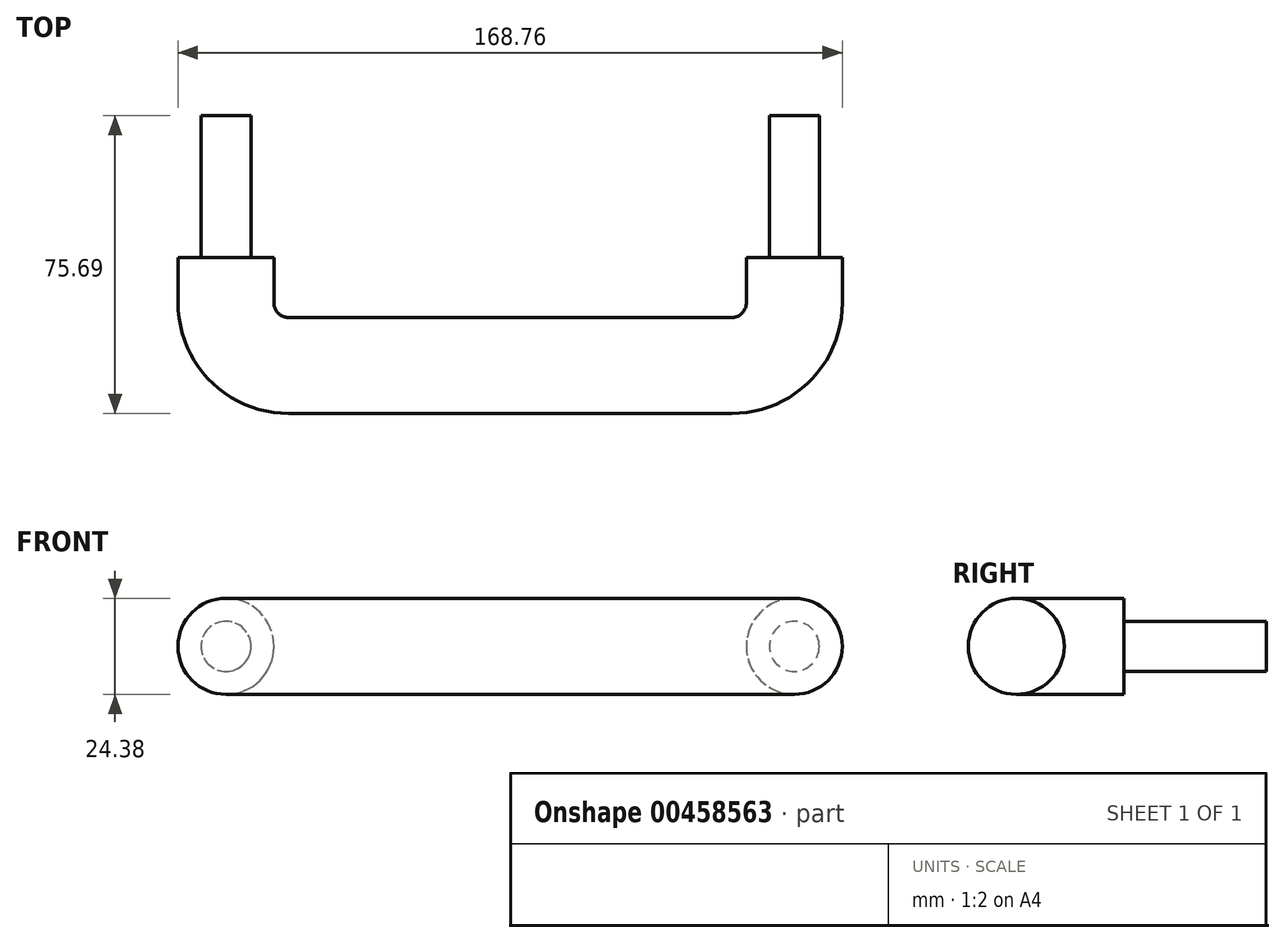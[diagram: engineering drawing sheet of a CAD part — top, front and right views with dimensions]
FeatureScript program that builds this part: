
annotation { "Feature Type Name" : "Feature", "Feature Type Description" : "" }
export const myFeature = defineFeature(function(context is Context, id is Id, definition is map)
    precondition{}
    {
        {
            var Q0;
            Q0=qCreatedBy(makeId("Top.planeOp"),FACE);
            var sketch = newSketch(context, id + "F0", { "sketchPlane" : qUnion([Q0])});
            skLineSegment(sketch, "E0", {"start": v(-72.19, 27.38) * mm, "end": v(-72.19, 15.87) * mm});
            skLineSegment(sketch, "E1", {"start": v(-56.31, 0) * mm, "end": v(56.31, 0) * mm});
            skLineSegment(sketch, "E2", {"start": v(72.19, 15.87) * mm, "end": v(72.19, 27.38) * mm});
            skLineSegment(sketch, "E3", {"start": v(-72.19, 27.38) * mm, "end": v(-72.19, 63.5) * mm});
            skLineSegment(sketch, "E4", {"start": v(-72.19, 63.5) * mm, "end": v(72.19, 63.5) * mm});
            skLineSegment(sketch, "E5", {"start": v(72.19, 27.38) * mm, "end": v(72.19, 63.5) * mm});
            skPoint(sketch, "E6.visualSharp", {"position": v(-72.19, 0) * mm});
            skArc(sketch, "E6.filletArc", {"start": v(-72.19, 15.87) * mm, "mid": v(-67.54, 4.65) * mm, "end": v(-56.31, 0) * mm});
            skPoint(sketch, "E7.visualSharp", {"position": v(72.19, 0) * mm});
            skArc(sketch, "E7.filletArc", {"start": v(56.31, 0) * mm, "mid": v(67.54, 4.65) * mm, "end": v(72.19, 15.87) * mm});
            skLineSegment(sketch, "E8", {"start": v(-72.19, 27.38) * mm, "end": v(72.19, 27.38) * mm, "construction": true});
            skSolve(sketch);
        }
        {
            var Q0;
            Q0=sQuery(id+"F0.wireOp",VERTEX,"E0.start");
            var Q1;
            Q1=sQuery(id+"F0.wireOp",EDGE,"E0");
            cPlane(context, id + "F1", {"entities" : qUnion([Q0, Q1]), "cplaneType" : CPlaneType.LINE_POINT, "offset" : 25.4 * mm, "width" : 152.4 * mm, "height" : 152.4 * mm});
        }
        {
            var Q0;
            Q0=qCreatedBy(id+"F1.planeOp",FACE);
            var sketch = newSketch(context, id + "F2", { "sketchPlane" : qUnion([Q0])});
            skCircle(sketch, "E9", {"center": v(72.19, 0) * mm, "radius": 12.2 * mm});
            skCircle(sketch, "E10", {"center": v(-72.19, 0) * mm, "radius": 6.35 * mm});
            skSolve(sketch);
        }
        {
            var Q0;
            Q0=makeQuery(id+"F2.imprint","IMPRINT",FACE,{"disambiguationData":[TD([[makeQuery(id+"F2.imprint","IMPRINT",EDGE,{"derivedFrom":sQuery(id+"F2.wireOp",EDGE,"E9")}),1.0]])]});
            var Q1;
            Q1=sQuery(id+"F0.wireOp",EDGE,"E2");
            var Q2;
            Q2=sQuery(id+"F0.wireOp",EDGE,"E7.filletArc");
            var Q3;
            Q3=sQuery(id+"F0.wireOp",EDGE,"E1");
            var Q4;
            Q4=sQuery(id+"F0.wireOp",EDGE,"E6.filletArc");
            var Q5;
            Q5=sQuery(id+"F0.wireOp",EDGE,"E0");
            sweep(context, id + "F3", {"profiles" : qUnion([Q0]), "path" : qUnion([Q1, Q2, Q3, Q4, Q5])});
        }
        {
            var Q0;
            Q0=makeQuery(id+"F2.imprint","IMPRINT",FACE,{"disambiguationData":[TD([[makeQuery(id+"F2.imprint","IMPRINT",EDGE,{"derivedFrom":sQuery(id+"F2.wireOp",EDGE,"E10")}),1.0]])]});
            var Q1;
            Q1=sQuery(id+"F0.wireOp",EDGE,"E3");
            var Q2;
            Q2=sQuery(id+"F0.wireOp",EDGE,"E0");
            var Q3;
            Q3=sQuery(id+"F0.wireOp",EDGE,"E6.filletArc");
            var Q4;
            Q4=sQuery(id+"F0.wireOp",EDGE,"E1");
            var Q5;
            Q5=sQuery(id+"F0.wireOp",EDGE,"E7.filletArc");
            var Q6;
            Q6=sQuery(id+"F0.wireOp",EDGE,"E2");
            var Q7;
            Q7=sQuery(id+"F0.wireOp",EDGE,"E5");
            sweep(context, id + "F4", {"operationType" : NewBodyOperationType.ADD, "profiles" : qUnion([Q0]), "path" : qUnion([Q1, Q2, Q3, Q4, Q5, Q6, Q7])});
        }
    });
